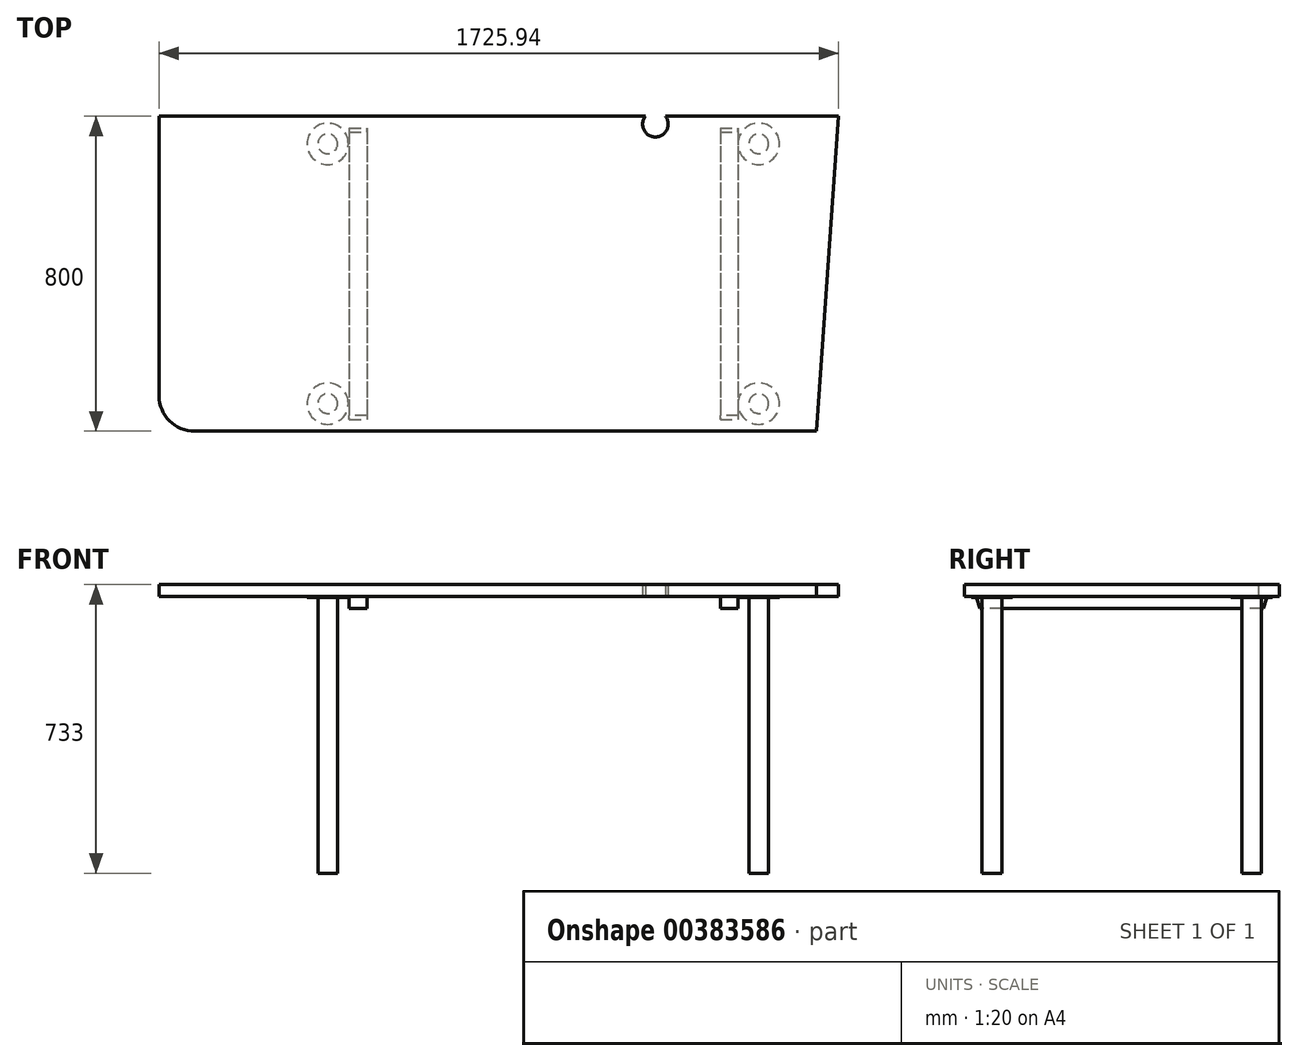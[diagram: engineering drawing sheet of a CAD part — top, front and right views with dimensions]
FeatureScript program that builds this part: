
annotation { "Feature Type Name" : "Feature", "Feature Type Description" : "" }
export const myFeature = defineFeature(function(context is Context, id is Id, definition is map)
    precondition{}
    {
        {
            var Q0;
            Q0=qCreatedBy(makeId("Top.planeOp"),FACE);
            var sketch = newSketch(context, id + "F0", { "sketchPlane" : qUnion([Q0])});
            skLineSegment(sketch, "E0.bottom", {"start": v(890.94, 400) * mm, "end": v(-835, 400) * mm});
            skLineSegment(sketch, "E0.top", {"start": v(835, -400) * mm, "end": v(-745, -400) * mm});
            skLineSegment(sketch, "E0.left", {"start": v(835, 400) * mm, "end": v(835, -400) * mm});
            skLineSegment(sketch, "E0.right", {"start": v(-835, 400) * mm, "end": v(-835, -310) * mm});
            skPoint(sketch, "E0.middle", {"position": v(0, 0) * mm});
            skLineSegment(sketch, "E1", {"start": v(835, -400) * mm, "end": v(890.94, 400) * mm});
            skPoint(sketch, "E2.visualSharp", {"position": v(-835, -400) * mm});
            skArc(sketch, "E2.filletArc", {"start": v(-835, -310) * mm, "mid": v(-808.64, -373.64) * mm, "end": v(-745, -400) * mm});
            skArc(sketch, "E3", {"start": v(400.32, 400) * mm, "mid": v(425.94, 347.5) * mm, "end": v(451.56, 400) * mm});
            skSolve(sketch);
        }
        {
            var Q0;
            Q0=makeQuery(id+"F0.imprint","IMPRINT",FACE,{"disambiguationData":[TD([[makeQuery(id+"F0.imprint","IMPRINT",EDGE,{"derivedFrom":sQuery(id+"F0.wireOp",EDGE,"E0.top")}),-1.0]])]});
            var Q1;
            {var subQ2=sQuery(id+"F0.wireOp",EDGE,"E0.left");Q1=makeQuery(id+"F0.imprint","IMPRINT",FACE,{"disambiguationData":[TD([[makeQuery(id+"F0.imprint","IMPRINT",EDGE,{"derivedFrom":subQ2}),1.0]])]});}
            extrude(context, id + "F1", {"entities" : qUnion([Q0, Q1]), "depth" : 30 * mm, "offsetDistance" : 25 * mm});
        }
        {
            var Q0;
            Q0=makeQuery(id+"F1.opExtrude","CAP_FACE",FACE,{"disambiguationData":[OSD([sQuery(id+"F0.wireOp",EDGE,"E0.bottom"),sQuery(id+"F0.wireOp",EDGE,"E0.top"),sQuery(id+"F0.wireOp",EDGE,"E0.left"),sQuery(id+"F0.wireOp",EDGE,"E0.right"),sQuery(id+"F0.wireOp",EDGE,"E2.filletArc"),sQuery(id+"F0.wireOp",EDGE,"E3")])],"isStart":true});
            var sketch = newSketch(context, id + "F2", { "sketchPlane" : qUnion([Q0])});
            skSolve(sketch);
        }
        {
            var Q0;
            Q0=makeQuery(id+"F2.imprint","IMPRINT",FACE,{"disambiguationData":[TD([[makeQuery(id+"F2.imprint","IMPRINT",EDGE,{"derivedFrom":makeQuery(id+"F1.opExtrude","CAP_EDGE",EDGE,{"disambiguationData":[OSD([sQuery(id+"F0.wireOp",EDGE,"E0.top")])],"isStart":true})}),1.0]])]});
            var sketch = newSketch(context, id + "F3", { "sketchPlane" : qUnion([Q0])});
            skLineSegment(sketch, "E4.bottom", {"start": v(590.94, -370) * mm, "end": v(635.94, -370) * mm});
            skLineSegment(sketch, "E4.top", {"start": v(590.94, 370) * mm, "end": v(635.94, 370) * mm});
            skLineSegment(sketch, "E4.left", {"start": v(590.94, -370) * mm, "end": v(590.94, 370) * mm});
            skLineSegment(sketch, "E4.right", {"start": v(635.94, -370) * mm, "end": v(635.94, 370) * mm});
            skLineSegment(sketch, "E5.0", {"start": v(835, 400) * mm, "end": v(-745, 400) * mm, "construction": true});
            skLineSegment(sketch, "E6.0", {"start": v(890.94, -400) * mm, "end": v(451.56, -400) * mm, "construction": true});
            skLineSegment(sketch, "E7.0", {"start": v(400.32, -400) * mm, "end": v(-835, -400) * mm, "construction": true});
            skLineSegment(sketch, "E8", {"start": v(635.94, -370) * mm, "end": v(635.94, -400) * mm, "construction": true});
            skLineSegment(sketch, "E9", {"start": v(635.94, 370) * mm, "end": v(635.94, 400) * mm, "construction": true});
            skSolve(sketch);
        }
        {
            var Q0;
            Q0=makeQuery(id+"F3.imprint","IMPRINT",FACE,{"disambiguationData":[TD([[makeQuery(id+"F3.imprint","IMPRINT",EDGE,{"derivedFrom":sQuery(id+"F3.wireOp",EDGE,"E4.bottom")}),1.0]])]});
            extrude(context, id + "F4", {"entities" : qUnion([Q0]), "depth" : 30 * mm, "offsetDistance" : 25 * mm});
        }
        {
            var Q0;
            Q0=makeQuery(id+"F4.opExtrude","CAP_EDGE",EDGE,{"disambiguationData":[OSD([sQuery(id+"F3.wireOp",EDGE,"E4.top")])],"isStart":false});
            var Q1;
            Q1=makeQuery(id+"F4.opExtrude","CAP_EDGE",EDGE,{"disambiguationData":[OSD([sQuery(id+"F3.wireOp",EDGE,"E4.bottom")])],"isStart":false});
            chamfer(context, id + "F5", {"entities" : qUnion([Q0, Q1]), "chamferType" : ChamferType.TWO_OFFSETS, "width1" : 30 * mm, "oppositeDirection" : false, "width2" : 10 * mm, "tangentPropagation" : true});
        }
        {
            var Q0;
            Q0=makeQuery(id+"F4.opExtrude","SWEPT_BODY",BODY,{"disambiguationData":[OSD([sQuery(id+"F3.wireOp",EDGE,"E4.bottom"),sQuery(id+"F3.wireOp",EDGE,"E4.top"),sQuery(id+"F3.wireOp",EDGE,"E4.left"),sQuery(id+"F3.wireOp",EDGE,"E4.right")])]});
            var Q1;
            {var subQ0=sQuery(id+"F0.wireOp",EDGE,"E0.bottom");Q1=makeQuery(id+"F1.opExtrude","CAP_EDGE",EDGE,{"disambiguationData":[OSD([subQ0]),TDD([makeQuery(id+"F0.imprint","IMPRINT",EDGE,{"disambiguationData":[TD([[makeQuery(id+"F0.imprint","INTERSECT",VERTEX,{"derivedFrom":[subQ0,sQuery(id+"F0.wireOp",EDGE,"E0.right")]}),1.0]])],"derivedFrom":subQ0})])],"isStart":true});}
            var Q2;
            {var subQ0=sQuery(id+"F0.wireOp",EDGE,"E0.bottom");Q2=makeQuery(id+"F1.opExtrude","CAP_EDGE",EDGE,{"disambiguationData":[OSD([subQ0]),TDD([makeQuery(id+"F0.imprint","IMPRINT",EDGE,{"disambiguationData":[TD([[makeQuery(id+"F0.imprint","INTERSECT",VERTEX,{"derivedFrom":[subQ0,sQuery(id+"F0.wireOp",EDGE,"E0.right")]}),1.0]])],"derivedFrom":subQ0})])],"isStart":true});}
            transform(context, id + "F6", {"entities" : qUnion([Q0]), "transformType" : TransformType.TRANSLATION_DISTANCE, "transformDirection" : qUnion([Q2]), "distance" : 943 * mm, "makeCopy" : true});
        }
        {
            var Q0;
            Q0=makeQuery(id+"F2.imprint","IMPRINT",FACE,{"disambiguationData":[TD([[makeQuery(id+"F2.imprint","IMPRINT",EDGE,{"derivedFrom":makeQuery(id+"F1.opExtrude","CAP_EDGE",EDGE,{"disambiguationData":[OSD([sQuery(id+"F0.wireOp",EDGE,"E0.top")])],"isStart":true})}),1.0]])]});
            var sketch = newSketch(context, id + "F7", { "sketchPlane" : qUnion([Q0])});
            skCircle(sketch, "E10", {"center": v(688.44, 330) * mm, "radius": 52.5 * mm});
            skSolve(sketch);
        }
        {
            var Q0;
            Q0=makeQuery(id+"F7.imprint","IMPRINT",FACE,{"disambiguationData":[TD([[makeQuery(id+"F7.imprint","IMPRINT",EDGE,{"derivedFrom":sQuery(id+"F7.wireOp",EDGE,"E10")}),1.0]])]});
            extrude(context, id + "F8", {"entities" : qUnion([Q0]), "depth" : 3 * mm, "offsetDistance" : 25 * mm});
        }
        {
            var Q0;
            Q0=makeQuery(id+"F8.opExtrude","CAP_FACE",FACE,{"disambiguationData":[OSD([sQuery(id+"F7.wireOp",EDGE,"E10")])],"isStart":false});
            var sketch = newSketch(context, id + "F9", { "sketchPlane" : qUnion([Q0])});
            skCircle(sketch, "E11.0", {"center": v(688.44, 330) * mm, "radius": 52.5 * mm});
            skCircle(sketch, "E12", {"center": v(688.44, 330) * mm, "radius": 25 * mm});
            skSolve(sketch);
        }
        {
            var Q0;
            Q0=makeQuery(id+"F9.imprint","IMPRINT",FACE,{"disambiguationData":[TD([[makeQuery(id+"F9.imprint","IMPRINT",EDGE,{"derivedFrom":sQuery(id+"F9.wireOp",EDGE,"E12")}),1.0]])]});
            extrude(context, id + "F10", {"entities" : qUnion([Q0]), "operationType" : NewBodyOperationType.ADD, "depth" : 700 * mm, "offsetDistance" : 25 * mm});
        }
        {
            var Q0;
            Q0=makeQuery(id+"F8.opExtrude","SWEPT_BODY",BODY,{"disambiguationData":[OSD([sQuery(id+"F7.wireOp",EDGE,"E10")])]});
            var Q1;
            Q1=makeQuery(id+"F1.opExtrude","CAP_EDGE",EDGE,{"disambiguationData":[OSD([sQuery(id+"F0.wireOp",EDGE,"E0.right")])],"isStart":true});
            transform(context, id + "F11", {"entities" : qUnion([Q0]), "transformType" : TransformType.TRANSLATION_DISTANCE, "transformDirection" : qUnion([Q1]), "distance" : 660 * mm, "oppositeDirection" : true, "makeCopy" : true});
        }
        {
            var Q0;
            Q0=makeQuery(id+"F8.opExtrude","SWEPT_BODY",BODY,{"disambiguationData":[OSD([sQuery(id+"F7.wireOp",EDGE,"E10")])]});
            var Q1;
            Q1=makeQuery(id+"F11.opPattern","COPY",BODY,{"derivedFrom":makeQuery(id+"F8.opExtrude","SWEPT_BODY",BODY,{"disambiguationData":[OSD([sQuery(id+"F7.wireOp",EDGE,"E10")])]}),"instanceName":"1"});
            var Q2;
            {var subQ0=sQuery(id+"F0.wireOp",EDGE,"E0.bottom");Q2=makeQuery(id+"F1.opExtrude","CAP_EDGE",EDGE,{"disambiguationData":[OSD([subQ0]),TDD([makeQuery(id+"F0.imprint","IMPRINT",EDGE,{"disambiguationData":[TD([[makeQuery(id+"F0.imprint","INTERSECT",VERTEX,{"derivedFrom":[subQ0,sQuery(id+"F0.wireOp",EDGE,"E0.right")]}),1.0]])],"derivedFrom":subQ0})])],"isStart":true});}
            transform(context, id + "F12", {"entities" : qUnion([Q0, Q1]), "transformType" : TransformType.TRANSLATION_DISTANCE, "transformDirection" : qUnion([Q2]), "distance" : 1095 * mm, "makeCopy" : true});
        }
    });
